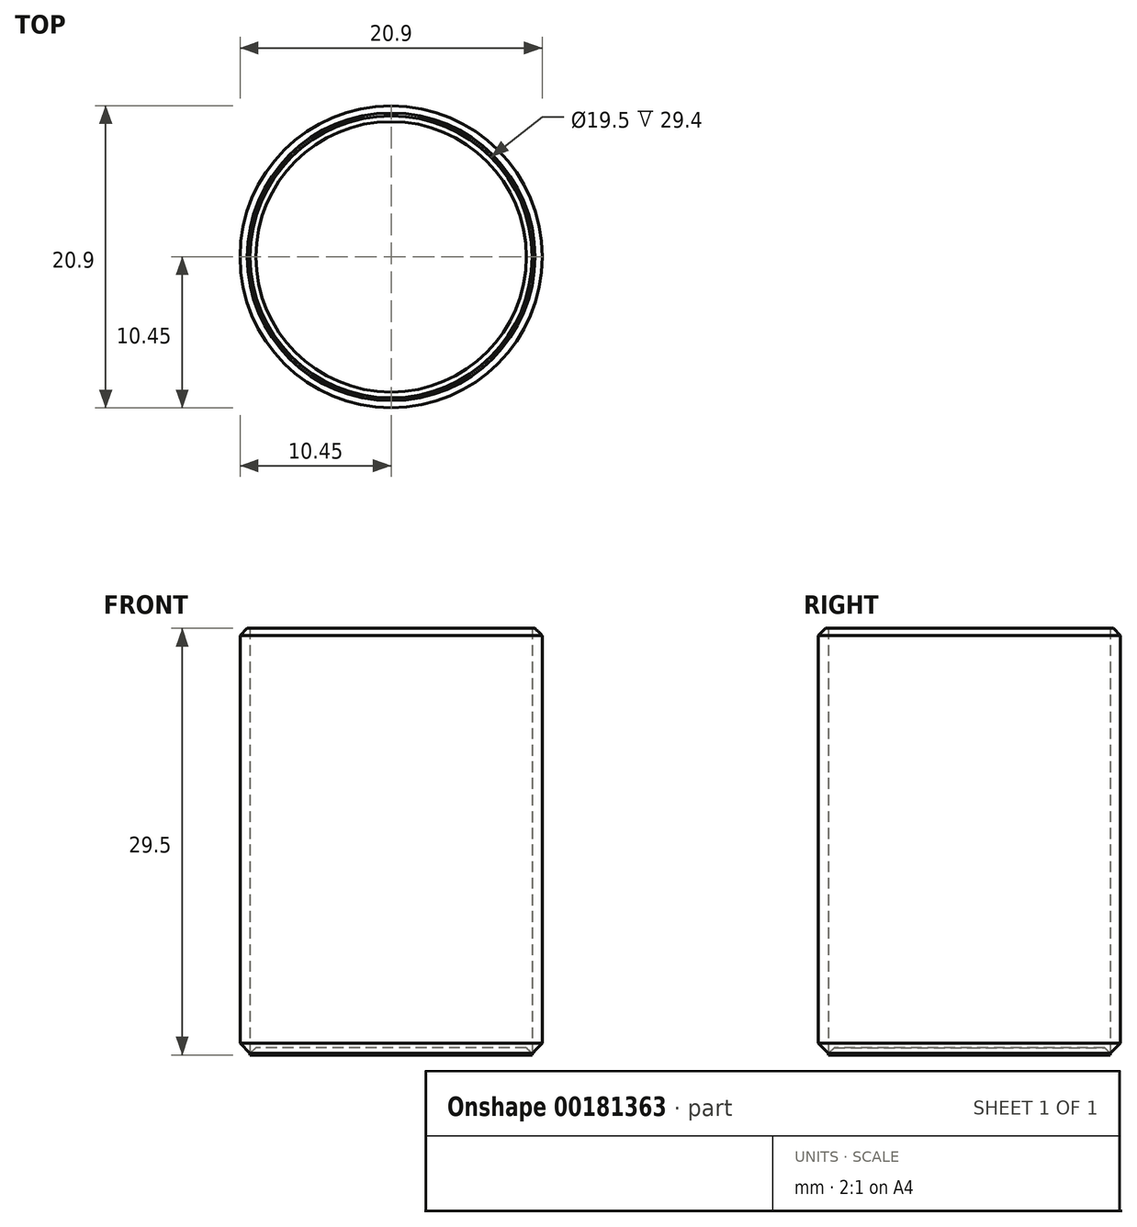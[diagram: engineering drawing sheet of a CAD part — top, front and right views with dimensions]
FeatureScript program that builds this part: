
annotation { "Feature Type Name" : "Feature", "Feature Type Description" : "" }
export const myFeature = defineFeature(function(context is Context, id is Id, definition is map)
    precondition{}
    {
        {
            var Q0;
            Q0=qCreatedBy(makeId("Top.planeOp"),FACE);
            var sketch = newSketch(context, id + "F0", { "sketchPlane" : qUnion([Q0])});
            skCircle(sketch, "E0", {"center": v(0, 0) * mm, "radius": 9.75 * mm});
            skCircle(sketch, "E1.0", {"center": v(0, 0) * mm, "radius": 10.45 * mm});
            skSolve(sketch);
        }
        {
            var Q0;
            Q0=makeQuery(id+"F0.imprint","IMPRINT",FACE,{"disambiguationData":[TD([[makeQuery(id+"F0.imprint","IMPRINT",EDGE,{"derivedFrom":sQuery(id+"F0.wireOp",EDGE,"E0")}),1.0]])]});
            extrude(context, id + "F1", {"entities" : qUnion([Q0]), "depth" : 0.5 * mm});
        }
        {
            var Q0;
            Q0=makeQuery(id+"F0.imprint","IMPRINT",FACE,{"disambiguationData":[TD([[makeQuery(id+"F0.imprint","IMPRINT",EDGE,{"derivedFrom":sQuery(id+"F0.wireOp",EDGE,"E0")}),-1.0]])]});
            extrude(context, id + "F2", {"entities" : qUnion([Q0]), "depth" : (28 + 1.5) * mm});
        }
        {
            var Q0;
            Q0=makeQuery(id+"F2.opExtrude","CAP_EDGE",EDGE,{"disambiguationData":[OSD([sQuery(id+"F0.wireOp",EDGE,"E1.0")])],"isStart":false});
            chamfer(context, id + "F3", {"entities" : qUnion([Q0]), "width" : 0.5 * mm, "tangentPropagation" : true});
        }
        {
            var Q0;
            Q0=makeQuery(id+"F1.opExtrude","CAP_EDGE",EDGE,{"disambiguationData":[OSD([sQuery(id+"F0.wireOp",EDGE,"E0")])],"isStart":false});
            chamfer(context, id + "F4", {"entities" : qUnion([Q0]), "width" : 0.4 * mm, "tangentPropagation" : true});
        }
        {
            var Q0;
            Q0=makeQuery(id+"F2.opExtrude","CAP_EDGE",EDGE,{"disambiguationData":[OSD([sQuery(id+"F0.wireOp",EDGE,"E1.0")])],"isStart":true});
            chamfer(context, id + "F5", {"entities" : qUnion([Q0]), "width" : 0.8 * mm, "tangentPropagation" : true});
        }
    });
